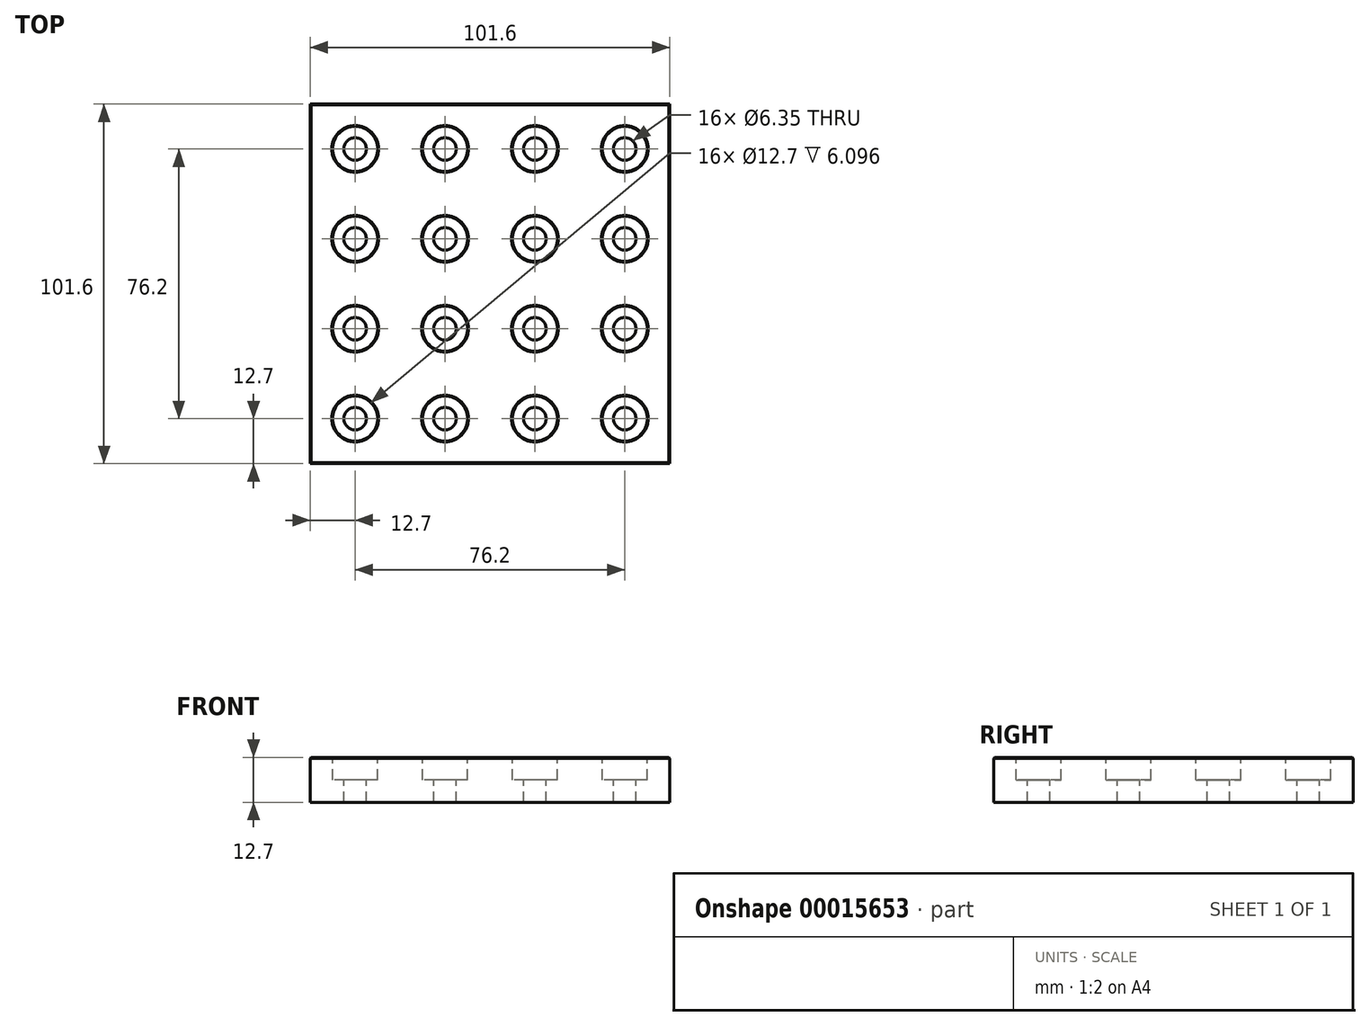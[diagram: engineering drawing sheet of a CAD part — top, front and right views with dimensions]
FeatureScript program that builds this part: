
annotation { "Feature Type Name" : "Feature", "Feature Type Description" : "" }
export const myFeature = defineFeature(function(context is Context, id is Id, definition is map)
    precondition{}
    {
        {
            var Q0;
            Q0=qCreatedBy(makeId("Top.planeOp"),FACE);
            var sketch = newSketch(context, id + "F0", { "sketchPlane" : qUnion([Q0])});
            skLineSegment(sketch, "E0.rect.bottom", {"start": v(50.8, 50.8) * mm, "end": v(-50.8, 50.8) * mm});
            skLineSegment(sketch, "E0.rect.top", {"start": v(50.8, -50.8) * mm, "end": v(-50.8, -50.8) * mm});
            skLineSegment(sketch, "E0.rect.left", {"start": v(50.8, 50.8) * mm, "end": v(50.8, -50.8) * mm});
            skLineSegment(sketch, "E0.rect.right", {"start": v(-50.8, 50.8) * mm, "end": v(-50.8, -50.8) * mm});
            skPoint(sketch, "E0.rect.middle", {"position": v(0, 0) * mm});
            skSolve(sketch);
        }
        {
            var Q0;
            Q0 = qSketchRegion(id + "F0", true);
            extrude(context, id + "F1", {"entities" : qUnion([Q0]), "endBound" : BoundingType.SYMMETRIC, "depth" : 12.7 * mm});
        }
        {
            var Q0;
            Q0=makeQuery(id+"F1.opExtrude","CAP_FACE",FACE,{"disambiguationData":[OSD([sQuery(id+"F0.wireOp",EDGE,"E0.rect.bottom"),sQuery(id+"F0.wireOp",EDGE,"E0.rect.top"),sQuery(id+"F0.wireOp",EDGE,"E0.rect.left"),sQuery(id+"F0.wireOp",EDGE,"E0.rect.right")])],"isStart":false});
            var sketch = newSketch(context, id + "F2", { "sketchPlane" : qUnion([Q0])});
            skPoint(sketch, "E1", {"position": v(-38.1, -38.1) * mm});
            skPoint(sketch, "E2", {"position": v(45.06, -38.32) * mm});
            skPoint(sketch, "E3.0.1.0", {"position": v(-38.1, -12.7) * mm});
            skPoint(sketch, "E3.0.2.0", {"position": v(-38.1, 12.7) * mm});
            skPoint(sketch, "E3.0.3.0", {"position": v(-38.1, 38.1) * mm});
            skPoint(sketch, "E3.1.0.0", {"position": v(-12.7, -38.1) * mm});
            skPoint(sketch, "E3.1.1.0", {"position": v(-12.7, -12.7) * mm});
            skPoint(sketch, "E3.1.2.0", {"position": v(-12.7, 12.7) * mm});
            skPoint(sketch, "E3.1.3.0", {"position": v(-12.7, 38.1) * mm});
            skPoint(sketch, "E3.2.0.0", {"position": v(12.7, -38.1) * mm});
            skPoint(sketch, "E3.2.1.0", {"position": v(12.7, -12.7) * mm});
            skPoint(sketch, "E3.2.2.0", {"position": v(12.7, 12.7) * mm});
            skPoint(sketch, "E3.2.3.0", {"position": v(12.7, 38.1) * mm});
            skPoint(sketch, "E3.3.0.0", {"position": v(38.1, -38.1) * mm});
            skPoint(sketch, "E3.3.1.0", {"position": v(38.1, -12.7) * mm});
            skPoint(sketch, "E3.3.2.0", {"position": v(38.1, 12.7) * mm});
            skPoint(sketch, "E3.3.3.0", {"position": v(38.1, 38.1) * mm});
            skLineSegment(sketch, "E3.direction1", {"start": v(-38.1, -38.1) * mm, "end": v(-12.7, -38.1) * mm, "construction": true});
            skLineSegment(sketch, "E3.direction2", {"start": v(-38.1, -38.1) * mm, "end": v(-38.1, -12.7) * mm, "construction": true});
            skSolve(sketch);
        }
        {
            var Q0;
            Q0=sQuery(id+"F2.wireOp",VERTEX,"E1");
            var Q1;
            Q1=sQuery(id+"F2.wireOp",VERTEX,"E3.0.1.0");
            var Q2;
            Q2=sQuery(id+"F2.wireOp",VERTEX,"E3.0.2.0");
            var Q3;
            Q3=sQuery(id+"F2.wireOp",VERTEX,"E3.0.3.0");
            var Q4;
            Q4=sQuery(id+"F2.wireOp",VERTEX,"E3.1.0.0");
            var Q5;
            Q5=sQuery(id+"F2.wireOp",VERTEX,"E3.1.1.0");
            var Q6;
            Q6=sQuery(id+"F2.wireOp",VERTEX,"E3.1.2.0");
            var Q7;
            Q7=sQuery(id+"F2.wireOp",VERTEX,"E3.1.3.0");
            var Q8;
            Q8=sQuery(id+"F2.wireOp",VERTEX,"E3.2.0.0");
            var Q9;
            Q9=sQuery(id+"F2.wireOp",VERTEX,"E3.2.1.0");
            var Q10;
            Q10=sQuery(id+"F2.wireOp",VERTEX,"E3.2.2.0");
            var Q11;
            Q11=sQuery(id+"F2.wireOp",VERTEX,"E3.2.3.0");
            var Q12;
            Q12=sQuery(id+"F2.wireOp",VERTEX,"E3.3.3.0");
            var Q13;
            Q13=sQuery(id+"F2.wireOp",VERTEX,"E3.3.2.0");
            var Q14;
            Q14=sQuery(id+"F2.wireOp",VERTEX,"E3.3.1.0");
            var Q15;
            Q15=sQuery(id+"F2.wireOp",VERTEX,"E3.3.0.0");
            var Q16;
            Q16=makeQuery(id+"F1.opExtrude","SWEPT_BODY",BODY,{"disambiguationData":[OSD([sQuery(id+"F0.wireOp",EDGE,"E0.rect.bottom"),sQuery(id+"F0.wireOp",EDGE,"E0.rect.top"),sQuery(id+"F0.wireOp",EDGE,"E0.rect.left"),sQuery(id+"F0.wireOp",EDGE,"E0.rect.right")])]});
            hole(context, id + "F3", {"style" : HoleStyle.C_BORE, "holeDiameter" : 6.35 * mm, "cBoreDiameter" : 12.7 * mm, "cBoreDepth" : 6.35 * mm, "endStyle" : HoleEndStyle.THROUGH, "locations" : qUnion([Q0, Q1, Q2, Q3, Q4, Q5, Q6, Q7, Q8, Q9, Q10, Q11, Q12, Q13, Q14, Q15]), "scope" : qUnion([Q16])});
        }
        {
            var Q0;
            Q0=makeQuery(id+"F1.opExtrude","CAP_FACE",FACE,{"disambiguationData":[OSD([sQuery(id+"F0.wireOp",EDGE,"E0.rect.bottom"),sQuery(id+"F0.wireOp",EDGE,"E0.rect.top"),sQuery(id+"F0.wireOp",EDGE,"E0.rect.left"),sQuery(id+"F0.wireOp",EDGE,"E0.rect.right")])],"isStart":false});
            chamfer(context, id + "F4", {"entities" : qUnion([Q0]), "width" : 0.25 * mm, "tangentPropagation" : true});
        }
    });
